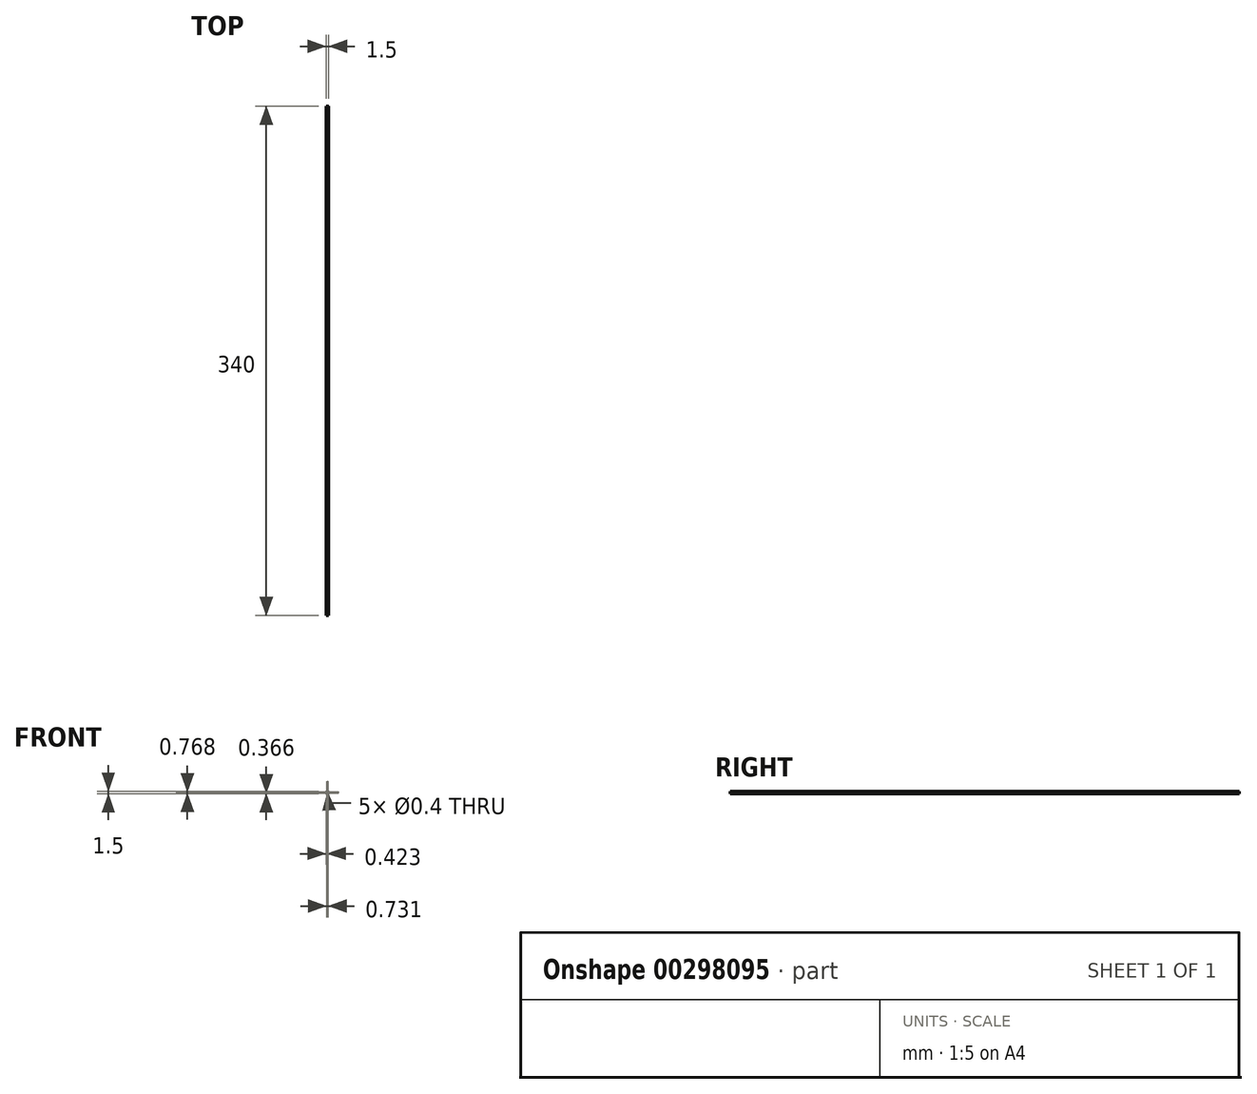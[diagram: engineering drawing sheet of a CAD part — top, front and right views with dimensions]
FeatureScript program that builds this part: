
annotation { "Feature Type Name" : "Feature", "Feature Type Description" : "" }
export const myFeature = defineFeature(function(context is Context, id is Id, definition is map)
    precondition{}
    {
        {
            var Q0;
            Q0=qCreatedBy(makeId("Front.planeOp"),FACE);
            var sketch = newSketch(context, id + "F0", { "sketchPlane" : qUnion([Q0])});
            skCircle(sketch, "E0", {"center": v(0.4, 0) * mm, "radius": 0.2 * mm});
            skCircle(sketch, "E1.1.0", {"center": v(0.12, 0.38) * mm, "radius": 0.2 * mm});
            skCircle(sketch, "E1.2.0", {"center": v(-0.33, 0.24) * mm, "radius": 0.2 * mm});
            skCircle(sketch, "E1.3.0", {"center": v(-0.33, -0.24) * mm, "radius": 0.2 * mm});
            skCircle(sketch, "E1.4.0", {"center": v(0.12, -0.38) * mm, "radius": 0.2 * mm});
            skPoint(sketch, "E1.center", {"position": v(0, 0) * mm});
            skCircle(sketch, "E2", {"center": v(0, 0) * mm, "radius": 0.75 * mm});
            skSolve(sketch);
        }
        {
            var Q0;
            Q0=makeQuery(id+"F0.imprint","IMPRINT",FACE,{"disambiguationData":[TD([[makeQuery(id+"F0.imprint","IMPRINT",EDGE,{"derivedFrom":sQuery(id+"F0.wireOp",EDGE,"E0")}),-1.0]])]});
            extrude(context, id + "F1", {"entities" : qUnion([Q0]), "depth" : 340 * mm});
        }
    });
